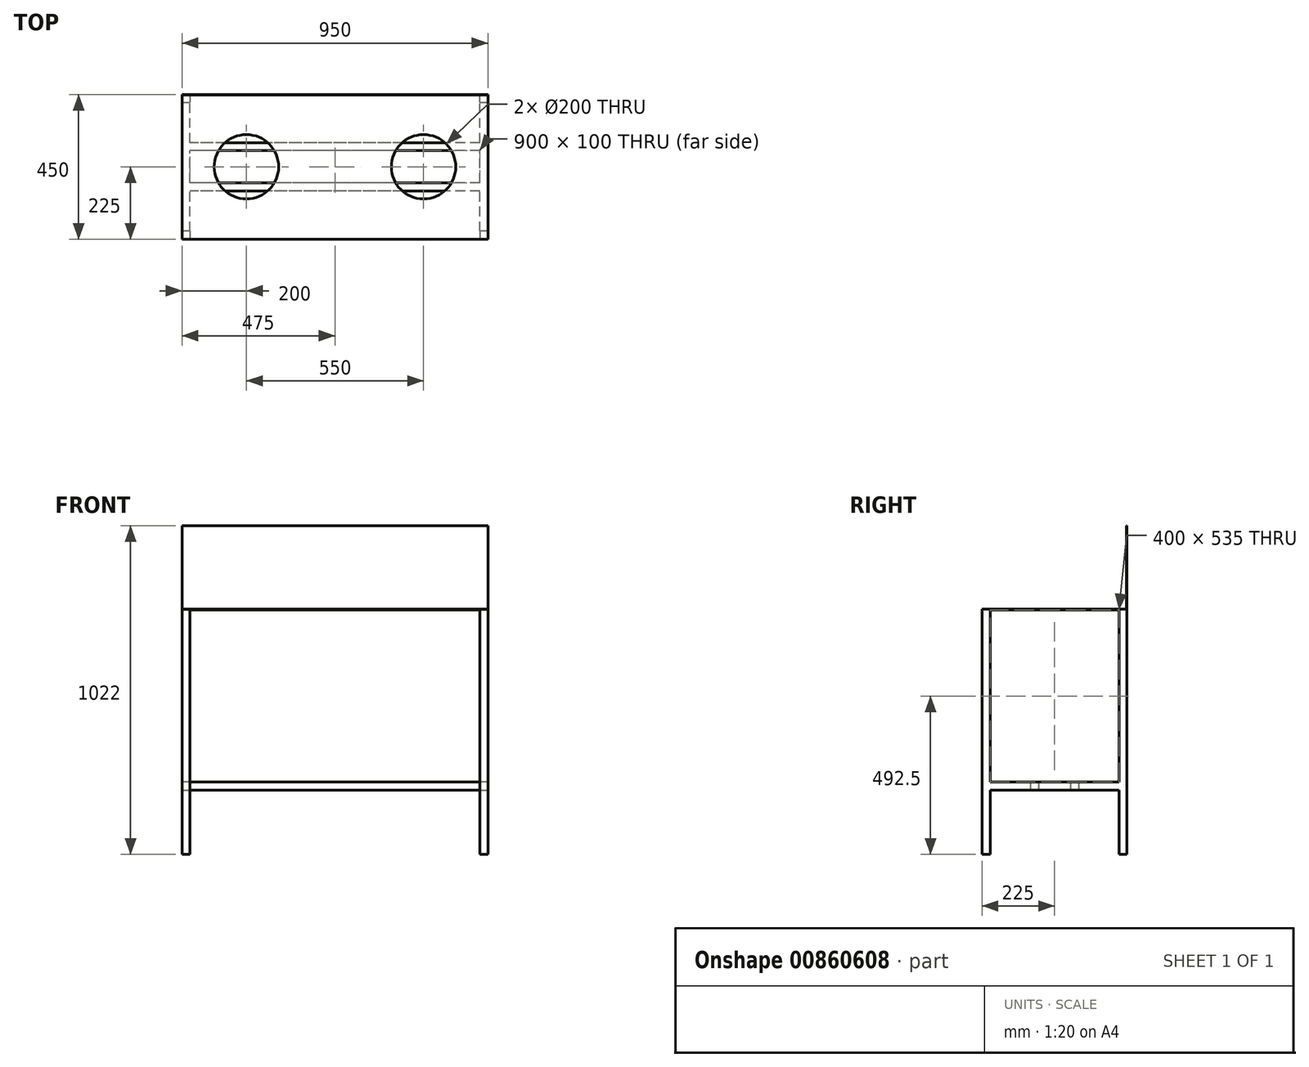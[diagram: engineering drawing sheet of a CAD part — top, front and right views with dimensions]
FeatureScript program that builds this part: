
annotation { "Feature Type Name" : "Feature", "Feature Type Description" : "" }
export const myFeature = defineFeature(function(context is Context, id is Id, definition is map)
    precondition{}
    {
        {
            var Q0;
            Q0=qCreatedBy(makeId("Top.planeOp"),FACE);
            var sketch = newSketch(context, id + "F0", { "sketchPlane" : qUnion([Q0])});
            skLineSegment(sketch, "E0.bottom", {"start": v(-475, -200) * mm, "end": v(-450, -200) * mm});
            skLineSegment(sketch, "E0.top", {"start": v(-475, -225) * mm, "end": v(-450, -225) * mm});
            skLineSegment(sketch, "E0.left", {"start": v(-475, -200) * mm, "end": v(-475, -225) * mm});
            skLineSegment(sketch, "E0.right", {"start": v(-450, -200) * mm, "end": v(-450, -225) * mm});
            skLineSegment(sketch, "E1.bottom", {"start": v(-475, 225) * mm, "end": v(-450, 225) * mm});
            skLineSegment(sketch, "E1.top", {"start": v(-475, 200) * mm, "end": v(-450, 200) * mm});
            skLineSegment(sketch, "E1.left", {"start": v(-475, 225) * mm, "end": v(-475, 200) * mm});
            skLineSegment(sketch, "E1.right", {"start": v(-450, 225) * mm, "end": v(-450, 200) * mm});
            skLineSegment(sketch, "E2.bottom", {"start": v(450, 200) * mm, "end": v(475, 200) * mm});
            skLineSegment(sketch, "E2.top", {"start": v(450, 225) * mm, "end": v(475, 225) * mm});
            skLineSegment(sketch, "E2.left", {"start": v(450, 200) * mm, "end": v(450, 225) * mm});
            skLineSegment(sketch, "E2.right", {"start": v(475, 200) * mm, "end": v(475, 225) * mm});
            skLineSegment(sketch, "E3.bottom", {"start": v(450, -200) * mm, "end": v(475, -200) * mm});
            skLineSegment(sketch, "E3.top", {"start": v(450, -225) * mm, "end": v(475, -225) * mm});
            skLineSegment(sketch, "E3.left", {"start": v(450, -200) * mm, "end": v(450, -225) * mm});
            skLineSegment(sketch, "E3.right", {"start": v(475, -200) * mm, "end": v(475, -225) * mm});
            skLineSegment(sketch, "E4", {"start": v(0, 81.35) * mm, "end": v(0, -82.17) * mm, "construction": true});
            skLineSegment(sketch, "E5", {"start": v(-92, 0) * mm, "end": v(93.65, 0) * mm, "construction": true});
            skSolve(sketch);
        }
        {
            var Q0;
            Q0=makeQuery(id+"F0.imprint","IMPRINT",FACE,{"disambiguationData":[TD([[makeQuery(id+"F0.imprint","IMPRINT",EDGE,{"derivedFrom":sQuery(id+"F0.wireOp",EDGE,"E1.bottom")}),-1.0]])]});
            extrude(context, id + "F1", {"entities" : qUnion([Q0]), "depth" : 760 * mm, "offsetDistance" : 25.4 * mm});
        }
        {
            var Q0;
            Q0=makeQuery(id+"F0.imprint","IMPRINT",FACE,{"disambiguationData":[TD([[makeQuery(id+"F0.imprint","IMPRINT",EDGE,{"derivedFrom":sQuery(id+"F0.wireOp",EDGE,"E3.bottom")}),-1.0]])]});
            var Q1;
            Q1=makeQuery(id+"F0.imprint","IMPRINT",FACE,{"disambiguationData":[TD([[makeQuery(id+"F0.imprint","IMPRINT",EDGE,{"derivedFrom":sQuery(id+"F0.wireOp",EDGE,"E2.bottom")}),1.0]])]});
            var Q2;
            Q2=makeQuery(id+"F0.imprint","IMPRINT",FACE,{"disambiguationData":[TD([[makeQuery(id+"F0.imprint","IMPRINT",EDGE,{"derivedFrom":sQuery(id+"F0.wireOp",EDGE,"E0.bottom")}),-1.0]])]});
            extrude(context, id + "F2", {"entities" : qUnion([Q0, Q1, Q2]), "operationType" : NewBodyOperationType.ADD, "depth" : 760 * mm, "offsetDistance" : 25.4 * mm});
        }
        {
            var Q0;
            Q0=makeQuery(id+"F1.opExtrude","CAP_FACE",FACE,{"disambiguationData":[OSD([sQuery(id+"F0.wireOp",EDGE,"E1.bottom"),sQuery(id+"F0.wireOp",EDGE,"E1.top"),sQuery(id+"F0.wireOp",EDGE,"E1.left"),sQuery(id+"F0.wireOp",EDGE,"E1.right")])],"isStart":false});
            var sketch = newSketch(context, id + "F3", { "sketchPlane" : qUnion([Q0])});
            skLineSegment(sketch, "E6.bottom", {"start": v(-475, 225) * mm, "end": v(475, 225) * mm});
            skLineSegment(sketch, "E6.top", {"start": v(-475, -225) * mm, "end": v(475, -225) * mm});
            skLineSegment(sketch, "E6.left", {"start": v(-475, 225) * mm, "end": v(-475, -225) * mm});
            skLineSegment(sketch, "E6.right", {"start": v(475, 225) * mm, "end": v(475, -225) * mm});
            skSolve(sketch);
        }
        {
            var Q0;
            Q0 = qSketchRegion(id + "F3", true);
            extrude(context, id + "F4", {"entities" : qUnion([Q0]), "operationType" : NewBodyOperationType.ADD, "depth" : 2 * mm, "offsetDistance" : 25.4 * mm});
        }
        {
            var Q0;
            Q0=makeQuery(id+"F4.opExtrude","CAP_FACE",FACE,{"disambiguationData":[OSD([sQuery(id+"F3.wireOp",EDGE,"E6.bottom"),sQuery(id+"F3.wireOp",EDGE,"E6.top"),sQuery(id+"F3.wireOp",EDGE,"E6.left"),sQuery(id+"F3.wireOp",EDGE,"E6.right")])],"isStart":false});
            var sketch = newSketch(context, id + "F5", { "sketchPlane" : qUnion([Q0])});
            skLineSegment(sketch, "E7.bottom", {"start": v(-475, 225) * mm, "end": v(475, 225) * mm});
            skLineSegment(sketch, "E7.top", {"start": v(-475, 223) * mm, "end": v(475, 223) * mm});
            skLineSegment(sketch, "E7.left", {"start": v(-475, 225) * mm, "end": v(-475, 223) * mm});
            skLineSegment(sketch, "E7.right", {"start": v(475, 225) * mm, "end": v(475, 223) * mm});
            skSolve(sketch);
        }
        {
            var Q0;
            Q0 = qSketchRegion(id + "F5", true);
            extrude(context, id + "F6", {"entities" : qUnion([Q0]), "operationType" : NewBodyOperationType.ADD, "depth" : 260 * mm, "offsetDistance" : 25.4 * mm});
        }
        {
            var Q0;
            Q0=makeQuery(id+"F1.opExtrude","SWEPT_FACE",FACE,{"disambiguationData":[OSD([sQuery(id+"F0.wireOp",EDGE,"E1.top")])]});
            var sketch = newSketch(context, id + "F7", { "sketchPlane" : qUnion([Q0])});
            skLineSegment(sketch, "E8.bottom", {"start": v(-475, 225) * mm, "end": v(-450, 225) * mm});
            skLineSegment(sketch, "E8.top", {"start": v(-475, 200) * mm, "end": v(-450, 200) * mm});
            skLineSegment(sketch, "E8.left", {"start": v(-475, 225) * mm, "end": v(-475, 200) * mm});
            skLineSegment(sketch, "E8.right", {"start": v(-450, 225) * mm, "end": v(-450, 200) * mm});
            skLineSegment(sketch, "E9.bottom", {"start": v(450, 225) * mm, "end": v(475, 225) * mm});
            skLineSegment(sketch, "E9.top", {"start": v(450, 200) * mm, "end": v(475, 200) * mm});
            skLineSegment(sketch, "E9.left", {"start": v(450, 225) * mm, "end": v(450, 200) * mm});
            skLineSegment(sketch, "E9.right", {"start": v(475, 225) * mm, "end": v(475, 200) * mm});
            skSolve(sketch);
        }
        {
            var Q0;
            Q0 = qSketchRegion(id + "F7", true);
            extrude(context, id + "F8", {"entities" : qUnion([Q0]), "operationType" : NewBodyOperationType.ADD, "endBound" : BoundingType.UP_TO_NEXT, "depth" : 25.4 * mm, "offsetDistance" : 25.4 * mm});
        }
        {
            var Q0;
            Q0=makeQuery(id+"F8.boolean.opBoolean","MERGE",FACE,{"derivedFrom":[makeQuery(id+"F1.opExtrude","SWEPT_FACE",FACE,{"disambiguationData":[OSD([sQuery(id+"F0.wireOp",EDGE,"E1.right")])]}),makeQuery(id+"F8.opExtrude","SWEPT_FACE",FACE,{"disambiguationData":[OSD([sQuery(id+"F7.wireOp",EDGE,"E8.right")])]})]});
            var sketch = newSketch(context, id + "F9", { "sketchPlane" : qUnion([Q0])});
            skLineSegment(sketch, "E10.bottom", {"start": v(50, 225) * mm, "end": v(75, 225) * mm});
            skLineSegment(sketch, "E10.top", {"start": v(50, 200) * mm, "end": v(75, 200) * mm});
            skLineSegment(sketch, "E10.left", {"start": v(50, 225) * mm, "end": v(50, 200) * mm});
            skLineSegment(sketch, "E10.right", {"start": v(75, 225) * mm, "end": v(75, 200) * mm});
            skLineSegment(sketch, "E11.bottom", {"start": v(-75, 225) * mm, "end": v(-50, 225) * mm});
            skLineSegment(sketch, "E11.top", {"start": v(-75, 200) * mm, "end": v(-50, 200) * mm});
            skLineSegment(sketch, "E11.left", {"start": v(-75, 225) * mm, "end": v(-75, 200) * mm});
            skLineSegment(sketch, "E11.right", {"start": v(-50, 225) * mm, "end": v(-50, 200) * mm});
            skSolve(sketch);
        }
        {
            var Q0;
            Q0 = qSketchRegion(id + "F9", true);
            extrude(context, id + "F10", {"entities" : qUnion([Q0]), "operationType" : NewBodyOperationType.ADD, "depth" : 900 * mm, "offsetDistance" : 25.4 * mm});
        }
        {
            var Q0;
            Q0=makeQuery(id+"F4.opExtrude","CAP_FACE",FACE,{"disambiguationData":[OSD([sQuery(id+"F3.wireOp",EDGE,"E6.bottom"),sQuery(id+"F3.wireOp",EDGE,"E6.top"),sQuery(id+"F3.wireOp",EDGE,"E6.left"),sQuery(id+"F3.wireOp",EDGE,"E6.right")])],"isStart":false});
            var sketch = newSketch(context, id + "F11", { "sketchPlane" : qUnion([Q0])});
            skCircle(sketch, "E12", {"center": v(-275, 0) * mm, "radius": 100 * mm});
            skCircle(sketch, "E13", {"center": v(275, 0) * mm, "radius": 100 * mm});
            skSolve(sketch);
        }
        {
            var Q0;
            Q0 = qSketchRegion(id + "F11", true);
            extrude(context, id + "F12", {"entities" : qUnion([Q0]), "operationType" : NewBodyOperationType.REMOVE, "endBound" : BoundingType.UP_TO_NEXT, "oppositeDirection" : true, "depth" : 25.4 * mm, "offsetDistance" : 25.4 * mm});
        }
    });
